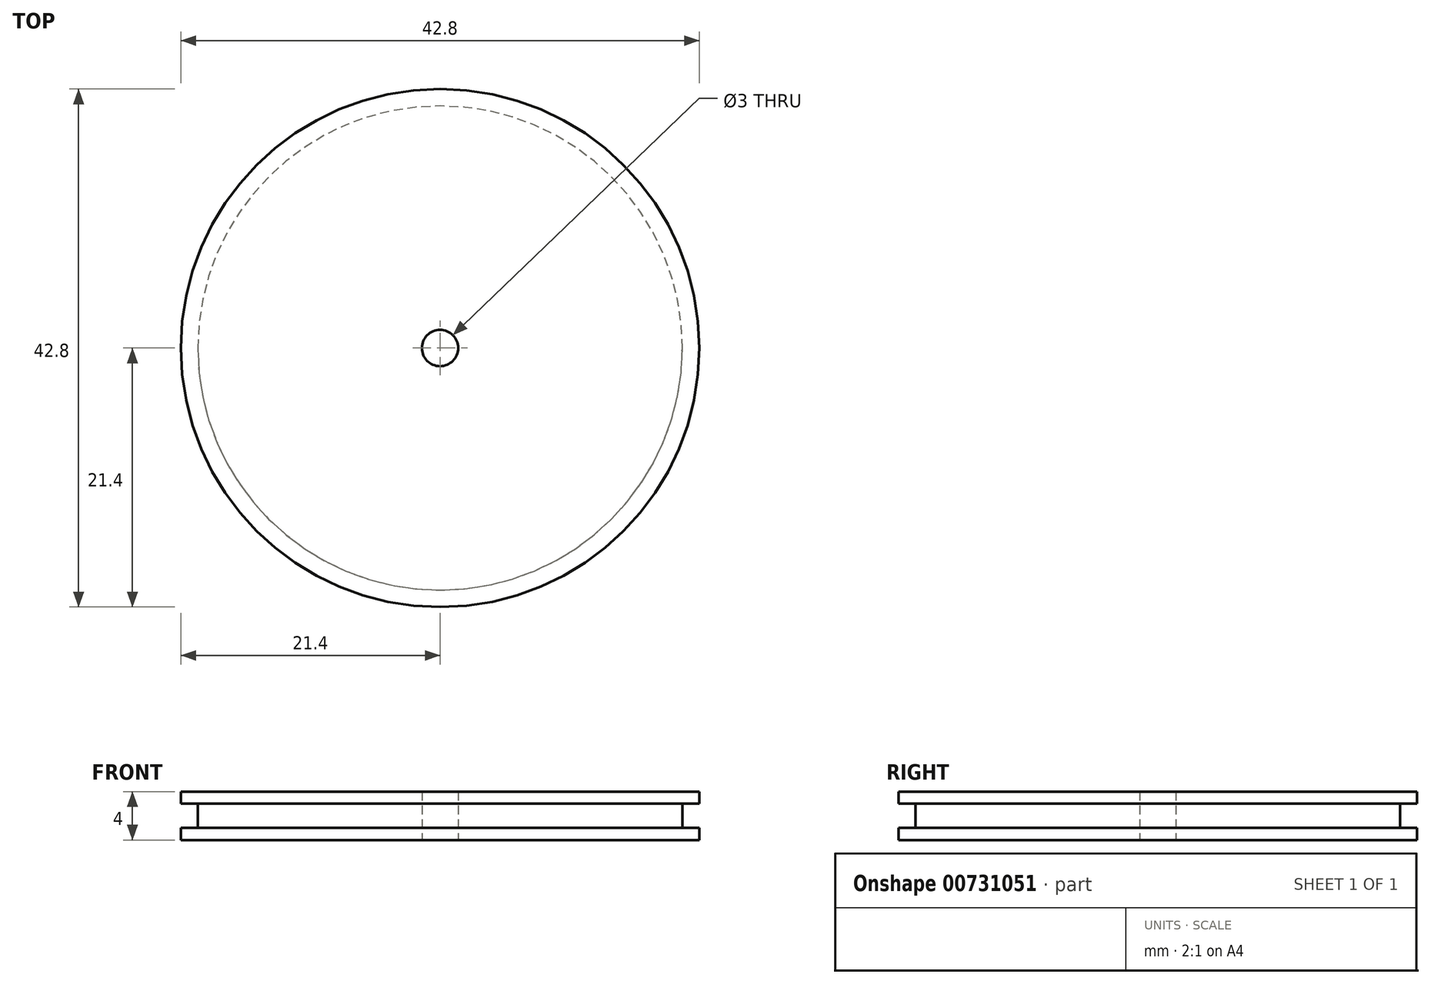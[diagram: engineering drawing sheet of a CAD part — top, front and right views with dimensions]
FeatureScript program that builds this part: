
annotation { "Feature Type Name" : "Feature", "Feature Type Description" : "" }
export const myFeature = defineFeature(function(context is Context, id is Id, definition is map)
    precondition{}
    {
        {
            var Q0;
            Q0=qCreatedBy(makeId("Top.planeOp"),FACE);
            var sketch = newSketch(context, id + "F0", { "sketchPlane" : qUnion([Q0])});
            skCircle(sketch, "E0", {"center": v(0, 0) * mm, "radius": 1.5 * mm});
            skCircle(sketch, "E1", {"center": v(0, 0) * mm, "radius": 20 * mm});
            skSolve(sketch);
        }
        {
            var Q0;
            Q0=makeQuery(id+"F0.imprint","IMPRINT",FACE,{"disambiguationData":[TD([[makeQuery(id+"F0.imprint","IMPRINT",EDGE,{"derivedFrom":sQuery(id+"F0.wireOp",EDGE,"E0")}),-1.0]])]});
            extrude(context, id + "F1", {"entities" : qUnion([Q0]), "depth" : 4 * mm, "offsetDistance" : 25 * mm});
        }
        {
            var Q0;
            Q0=makeQuery(id+"F1.opExtrude","CAP_FACE",FACE,{"disambiguationData":[OSD([sQuery(id+"F0.wireOp",EDGE,"E0"),sQuery(id+"F0.wireOp",EDGE,"E1")])],"isStart":false});
            var sketch = newSketch(context, id + "F2", { "sketchPlane" : qUnion([Q0])});
            skCircle(sketch, "E2", {"center": v(0, 0) * mm, "radius": 21.4 * mm});
            skSolve(sketch);
        }
        {
            var Q0;
            Q0=makeQuery(id+"F2.imprint","IMPRINT",FACE,{"disambiguationData":[TD([[makeQuery(id+"F2.imprint","IMPRINT",EDGE,{"derivedFrom":sQuery(id+"F2.wireOp",EDGE,"E2")}),1.0]])]});
            extrude(context, id + "F3", {"entities" : qUnion([Q0]), "operationType" : NewBodyOperationType.ADD, "oppositeDirection" : true, "depth" : 1 * mm, "offsetDistance" : 25 * mm});
        }
        {
            var Q0;
            Q0=makeQuery(id+"F1.opExtrude","CAP_FACE",FACE,{"disambiguationData":[OSD([sQuery(id+"F0.wireOp",EDGE,"E0"),sQuery(id+"F0.wireOp",EDGE,"E1")])],"isStart":true});
            var sketch = newSketch(context, id + "F4", { "sketchPlane" : qUnion([Q0])});
            skCircle(sketch, "E3", {"center": v(0, 0) * mm, "radius": 21.4 * mm});
            skSolve(sketch);
        }
        {
            var Q0;
            Q0=makeQuery(id+"F4.imprint","IMPRINT",FACE,{"disambiguationData":[TD([[makeQuery(id+"F4.imprint","IMPRINT",EDGE,{"derivedFrom":sQuery(id+"F4.wireOp",EDGE,"E3")}),1.0]])]});
            extrude(context, id + "F5", {"entities" : qUnion([Q0]), "operationType" : NewBodyOperationType.ADD, "oppositeDirection" : true, "depth" : 1 * mm, "offsetDistance" : 25 * mm});
        }
    });
